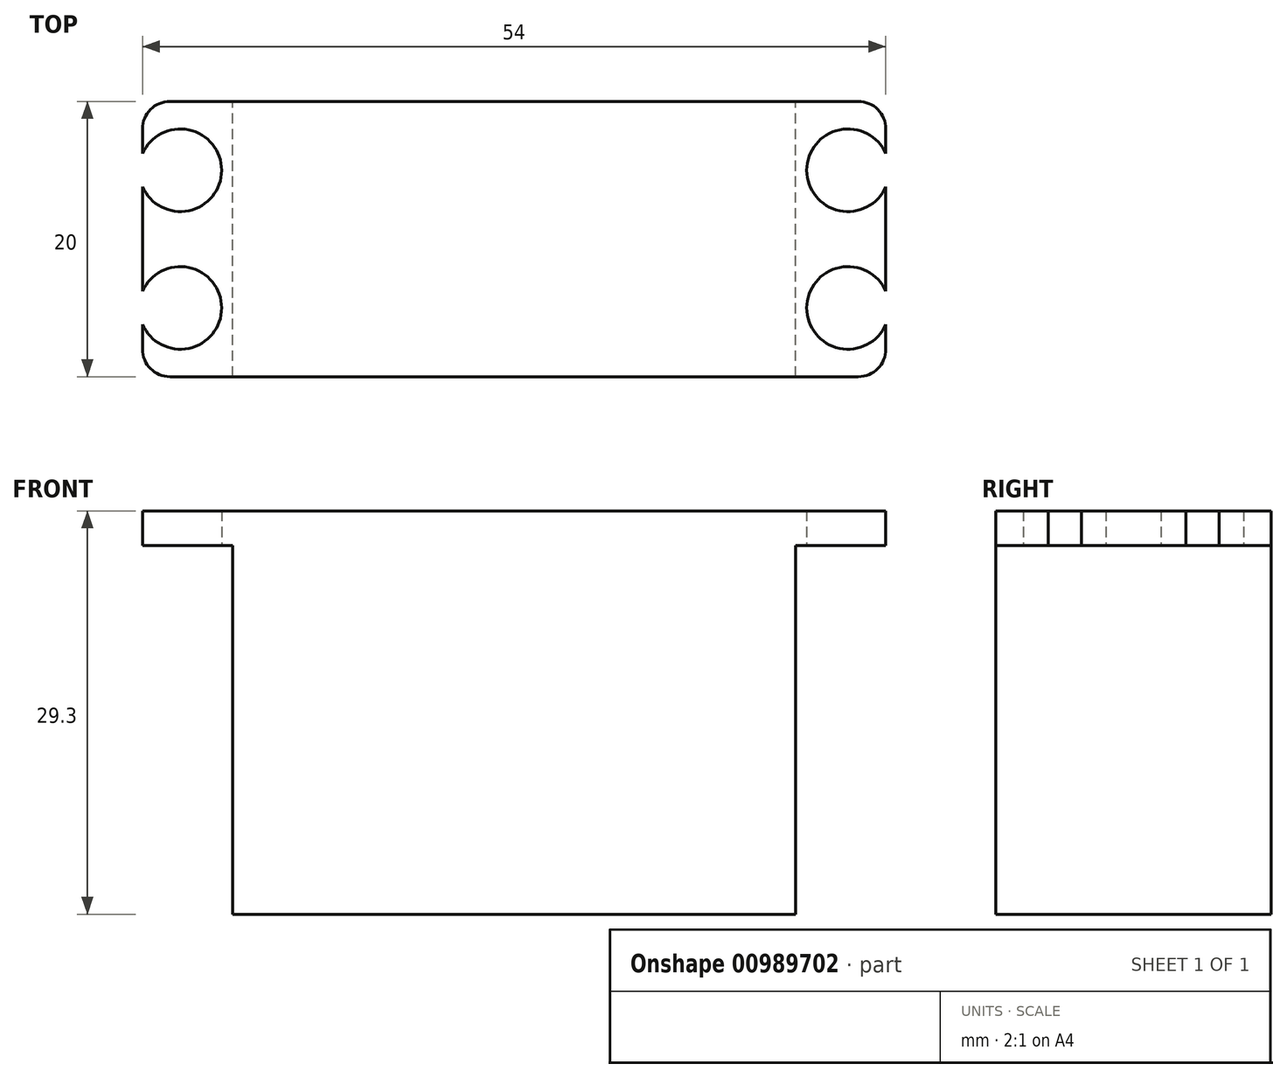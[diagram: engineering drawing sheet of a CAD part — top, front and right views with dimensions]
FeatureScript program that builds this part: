
annotation { "Feature Type Name" : "Feature", "Feature Type Description" : "" }
export const myFeature = defineFeature(function(context is Context, id is Id, definition is map)
    precondition{}
    {
        {
            var Q0;
            Q0=qCreatedBy(makeId("Top.planeOp"),FACE);
            var sketch = newSketch(context, id + "F0", { "sketchPlane" : qUnion([Q0])});
            skLineSegment(sketch, "E0.bottom", {"start": v(-20.45, -10) * mm, "end": v(20.45, -10) * mm});
            skLineSegment(sketch, "E0.top", {"start": v(-20.45, 10) * mm, "end": v(20.45, 10) * mm});
            skLineSegment(sketch, "E0.left", {"start": v(-20.45, -10) * mm, "end": v(-20.45, 10) * mm});
            skLineSegment(sketch, "E0.right", {"start": v(20.45, -10) * mm, "end": v(20.45, 10) * mm});
            skPoint(sketch, "E0.middle", {"position": v(0, 0) * mm});
            skLineSegment(sketch, "E1.bottom", {"start": v(24.25, -5) * mm, "end": v(-24.25, -5) * mm});
            skLineSegment(sketch, "E1.top", {"start": v(24.25, 5) * mm, "end": v(-24.25, 5) * mm});
            skLineSegment(sketch, "E1.left", {"start": v(24.25, -5) * mm, "end": v(24.25, 5) * mm});
            skLineSegment(sketch, "E1.right", {"start": v(-24.25, -5) * mm, "end": v(-24.25, 5) * mm});
            skCircle(sketch, "E2", {"center": v(-24.25, 5) * mm, "radius": 3 * mm});
            skLineSegment(sketch, "E3.bottom", {"start": v(-25, -10) * mm, "end": v(25, -10) * mm});
            skLineSegment(sketch, "E3.top", {"start": v(-25, 10) * mm, "end": v(25, 10) * mm});
            skLineSegment(sketch, "E3.left", {"start": v(-27, -8) * mm, "end": v(-27, 8) * mm});
            skLineSegment(sketch, "E3.right", {"start": v(27, -8) * mm, "end": v(27, 8) * mm});
            skCircle(sketch, "E4.MirrorC", {"center": v(24.25, 5) * mm, "radius": 3 * mm});
            skCircle(sketch, "E5.MirrorC", {"center": v(-24.25, -5) * mm, "radius": 3 * mm});
            skCircle(sketch, "E6.MirrorC", {"center": v(24.25, -5) * mm, "radius": 3 * mm});
            skPoint(sketch, "E7.visualSharp", {"position": v(-27, 10) * mm});
            skArc(sketch, "E7.filletArc", {"start": v(-25, 10) * mm, "mid": v(-26.41, 9.41) * mm, "end": v(-27, 8) * mm});
            skPoint(sketch, "E8.visualSharp", {"position": v(-27, -10) * mm});
            skArc(sketch, "E8.filletArc", {"start": v(-27, -8) * mm, "mid": v(-26.41, -9.41) * mm, "end": v(-25, -10) * mm});
            skPoint(sketch, "E9.visualSharp", {"position": v(27, -10) * mm});
            skArc(sketch, "E9.filletArc", {"start": v(25, -10) * mm, "mid": v(26.41, -9.41) * mm, "end": v(27, -8) * mm});
            skPoint(sketch, "E10.visualSharp", {"position": v(27, 10) * mm});
            skArc(sketch, "E10.filletArc", {"start": v(27, 8) * mm, "mid": v(26.41, 9.41) * mm, "end": v(25, 10) * mm});
            skSolve(sketch);
        }
        {
            var Q0;
            {var subQ0=sQuery(id+"F0.wireOp",EDGE,"E1.bottom");var subQ1=sQuery(id+"F0.wireOp",EDGE,"E0.left");var subQ2=makeQuery(id+"F0.imprint","INTERSECT",VERTEX,{"derivedFrom":[subQ1,subQ0]});Q0=makeQuery(id+"F0.imprint","IMPRINT",FACE,{"disambiguationData":[TD([[makeQuery(id+"F0.imprint","IMPRINT",EDGE,{"disambiguationData":[TD([[subQ2,-1.0]])],"derivedFrom":subQ1}),-1.0]])]});}
            var Q1;
            {var subQ0=sQuery(id+"F0.wireOp",EDGE,"E3.bottom");var subQ1=sQuery(id+"F0.wireOp",EDGE,"E0.left");var subQ2=makeQuery(id+"F0.imprint","INTERSECT",VERTEX,{"derivedFrom":[subQ1,subQ0]});Q1=makeQuery(id+"F0.imprint","IMPRINT",FACE,{"disambiguationData":[TD([[makeQuery(id+"F0.imprint","IMPRINT",EDGE,{"disambiguationData":[TD([[subQ2,-1.0]])],"derivedFrom":subQ1}),-1.0]])]});}
            var Q2;
            {var subQ0=sQuery(id+"F0.wireOp",EDGE,"E3.top");var subQ1=sQuery(id+"F0.wireOp",EDGE,"E0.left");var subQ2=makeQuery(id+"F0.imprint","INTERSECT",VERTEX,{"derivedFrom":[subQ1,subQ0]});Q2=makeQuery(id+"F0.imprint","IMPRINT",FACE,{"disambiguationData":[TD([[makeQuery(id+"F0.imprint","IMPRINT",EDGE,{"disambiguationData":[TD([[subQ2,1.0]])],"derivedFrom":subQ1}),-1.0]])]});}
            extrude(context, id + "F1", {"entities" : qUnion([Q0, Q1, Q2]), "oppositeDirection" : true, "depth" : 26.8 * mm, "offsetDistance" : 25 * mm});
        }
        {
            var Q0;
            {var subQ0=sQuery(id+"F0.wireOp",EDGE,"E3.top");var subQ1=sQuery(id+"F0.wireOp",EDGE,"E0.left");var subQ2=makeQuery(id+"F0.imprint","INTERSECT",VERTEX,{"derivedFrom":[subQ1,subQ0]});Q0=makeQuery(id+"F0.imprint","IMPRINT",FACE,{"disambiguationData":[TD([[makeQuery(id+"F0.imprint","IMPRINT",EDGE,{"disambiguationData":[TD([[subQ2,1.0]])],"derivedFrom":subQ1}),1.0]])]});}
            var Q1;
            {var subQ5=sQuery(id+"F0.wireOp",EDGE,"E1.bottom");var subQ6=sQuery(id+"F0.wireOp",EDGE,"E0.left");var subQ7=makeQuery(id+"F0.imprint","INTERSECT",VERTEX,{"derivedFrom":[subQ6,subQ5]});Q1=makeQuery(id+"F0.imprint","IMPRINT",FACE,{"disambiguationData":[TD([[makeQuery(id+"F0.imprint","IMPRINT",EDGE,{"disambiguationData":[TD([[subQ7,-1.0]])],"derivedFrom":subQ6}),1.0]])]});}
            var Q2;
            {var subQ0=sQuery(id+"F0.wireOp",EDGE,"E5.MirrorC");var subQ1=sQuery(id+"F0.wireOp",EDGE,"E1.right");var subQ2=makeQuery(id+"F0.imprint","INTERSECT",VERTEX,{"derivedFrom":[subQ1,subQ0]});Q2=makeQuery(id+"F0.imprint","IMPRINT",FACE,{"disambiguationData":[TD([[makeQuery(id+"F0.imprint","IMPRINT",EDGE,{"disambiguationData":[TD([[subQ2,-1.0]])],"derivedFrom":subQ1}),1.0]])]});}
            var Q3;
            {var subQ1=sQuery(id+"F0.wireOp",EDGE,"E3.bottom");var subQ5=sQuery(id+"F0.wireOp",EDGE,"E0.left");var subQ6=makeQuery(id+"F0.imprint","INTERSECT",VERTEX,{"derivedFrom":[subQ5,subQ1]});Q3=makeQuery(id+"F0.imprint","IMPRINT",FACE,{"disambiguationData":[TD([[makeQuery(id+"F0.imprint","IMPRINT",EDGE,{"disambiguationData":[TD([[subQ6,-1.0]])],"derivedFrom":subQ5}),1.0]])]});}
            var Q4;
            {var subQ0=sQuery(id+"F0.wireOp",EDGE,"E3.bottom");var subQ1=sQuery(id+"F0.wireOp",EDGE,"E0.left");var subQ2=makeQuery(id+"F0.imprint","INTERSECT",VERTEX,{"derivedFrom":[subQ1,subQ0]});Q4=makeQuery(id+"F0.imprint","IMPRINT",FACE,{"disambiguationData":[TD([[makeQuery(id+"F0.imprint","IMPRINT",EDGE,{"disambiguationData":[TD([[subQ2,-1.0]])],"derivedFrom":subQ1}),-1.0]])]});}
            var Q5;
            {var subQ0=sQuery(id+"F0.wireOp",EDGE,"E1.bottom");var subQ1=sQuery(id+"F0.wireOp",EDGE,"E0.left");var subQ2=makeQuery(id+"F0.imprint","INTERSECT",VERTEX,{"derivedFrom":[subQ1,subQ0]});Q5=makeQuery(id+"F0.imprint","IMPRINT",FACE,{"disambiguationData":[TD([[makeQuery(id+"F0.imprint","IMPRINT",EDGE,{"disambiguationData":[TD([[subQ2,-1.0]])],"derivedFrom":subQ1}),-1.0]])]});}
            var Q6;
            {var subQ1=sQuery(id+"F0.wireOp",EDGE,"E3.bottom");var subQ6=sQuery(id+"F0.wireOp",EDGE,"E0.right");var subQ9=makeQuery(id+"F0.imprint","INTERSECT",VERTEX,{"derivedFrom":[subQ6,subQ1]});Q6=makeQuery(id+"F0.imprint","IMPRINT",FACE,{"disambiguationData":[TD([[makeQuery(id+"F0.imprint","IMPRINT",EDGE,{"disambiguationData":[TD([[subQ9,-1.0]])],"derivedFrom":subQ6}),-1.0]])]});}
            var Q7;
            {var subQ0=sQuery(id+"F0.wireOp",EDGE,"E3.top");var subQ1=sQuery(id+"F0.wireOp",EDGE,"E0.left");var subQ2=makeQuery(id+"F0.imprint","INTERSECT",VERTEX,{"derivedFrom":[subQ1,subQ0]});Q7=makeQuery(id+"F0.imprint","IMPRINT",FACE,{"disambiguationData":[TD([[makeQuery(id+"F0.imprint","IMPRINT",EDGE,{"disambiguationData":[TD([[subQ2,1.0]])],"derivedFrom":subQ1}),-1.0]])]});}
            var Q8;
            {var subQ1=sQuery(id+"F0.wireOp",EDGE,"E3.top");var subQ5=sQuery(id+"F0.wireOp",EDGE,"E0.right");var subQ6=makeQuery(id+"F0.imprint","INTERSECT",VERTEX,{"derivedFrom":[subQ5,subQ1]});Q8=makeQuery(id+"F0.imprint","IMPRINT",FACE,{"disambiguationData":[TD([[makeQuery(id+"F0.imprint","IMPRINT",EDGE,{"disambiguationData":[TD([[subQ6,1.0]])],"derivedFrom":subQ5}),-1.0]])]});}
            var Q9;
            {var subQ6=sQuery(id+"F0.wireOp",EDGE,"E0.right");var subQ9=sQuery(id+"F0.wireOp",EDGE,"E1.bottom");var subQ10=makeQuery(id+"F0.imprint","INTERSECT",VERTEX,{"derivedFrom":[subQ6,subQ9]});Q9=makeQuery(id+"F0.imprint","IMPRINT",FACE,{"disambiguationData":[TD([[makeQuery(id+"F0.imprint","IMPRINT",EDGE,{"disambiguationData":[TD([[subQ10,-1.0]])],"derivedFrom":subQ6}),-1.0]])]});}
            var Q10;
            {var subQ0=sQuery(id+"F0.wireOp",EDGE,"E6.MirrorC");var subQ1=sQuery(id+"F0.wireOp",EDGE,"E1.left");var subQ2=makeQuery(id+"F0.imprint","INTERSECT",VERTEX,{"derivedFrom":[subQ1,subQ0]});Q10=makeQuery(id+"F0.imprint","IMPRINT",FACE,{"disambiguationData":[TD([[makeQuery(id+"F0.imprint","IMPRINT",EDGE,{"disambiguationData":[TD([[subQ2,-1.0]])],"derivedFrom":subQ1}),-1.0]])]});}
            extrude(context, id + "F2", {"entities" : qUnion([Q0, Q1, Q2, Q3, Q4, Q5, Q6, Q7, Q8, Q9, Q10]), "operationType" : NewBodyOperationType.ADD, "depth" : 2.5 * mm, "offsetDistance" : 25 * mm});
        }
    });
